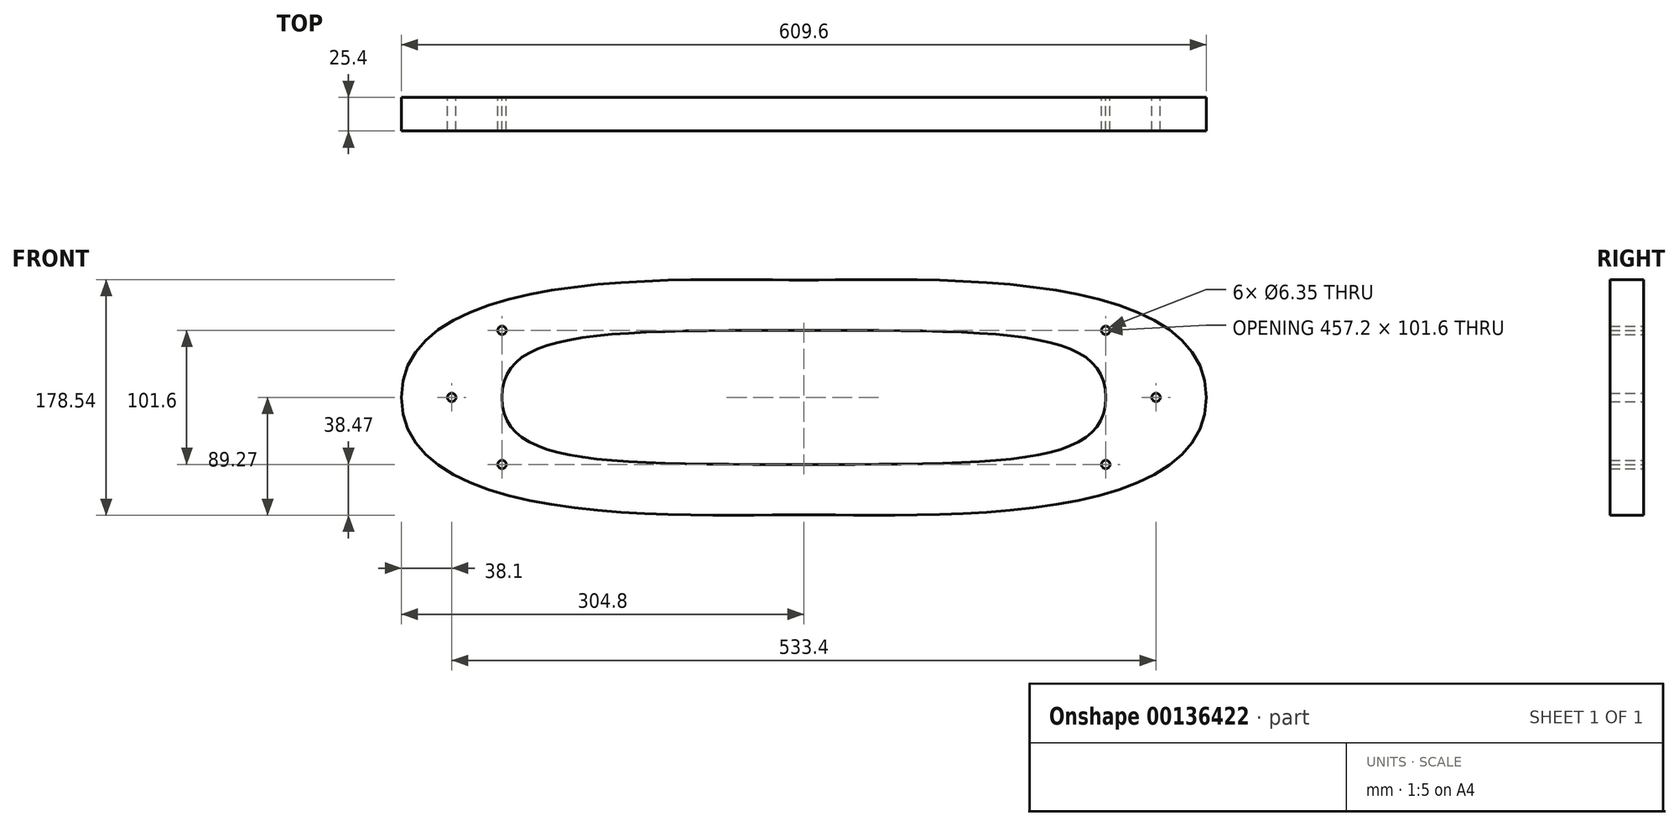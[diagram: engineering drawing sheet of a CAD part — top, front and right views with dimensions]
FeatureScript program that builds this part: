
annotation { "Feature Type Name" : "Feature", "Feature Type Description" : "" }
export const myFeature = defineFeature(function(context is Context, id is Id, definition is map)
    precondition{}
    {
        {
            var Q0;
            Q0=qCreatedBy(makeId("Front.planeOp"),FACE);
            var sketch = newSketch(context, id + "F0", { "sketchPlane" : qUnion([Q0])});
            skLineSegment(sketch, "E0.bottom", {"start": v(228.6, -101.6) * mm, "end": v(-228.6, -101.6) * mm, "construction": true});
            skLineSegment(sketch, "E0.top", {"start": v(228.6, 101.6) * mm, "end": v(-228.6, 101.6) * mm, "construction": true});
            skLineSegment(sketch, "E0.left", {"start": v(228.6, -101.6) * mm, "end": v(228.6, 101.6) * mm, "construction": true});
            skLineSegment(sketch, "E0.right", {"start": v(-228.6, -101.6) * mm, "end": v(-228.6, 101.6) * mm, "construction": true});
            skPoint(sketch, "E0.middle", {"position": v(0, 0) * mm});
            skLineSegment(sketch, "E1", {"start": v(-228.6, 0) * mm, "end": v(228.6, 0) * mm, "construction": true});
            skLineSegment(sketch, "E2", {"start": v(0, 101.6) * mm, "end": v(0, -101.6) * mm, "construction": true});
            skEllipse(sketch, "E3", {"center": v(0, 0) * mm, "majorRadius": 228.6 * mm, "minorRadius": 101.6 * mm, "majorAxis": v(1, 0), "construction": true});
            skLineSegment(sketch, "E4.0", {"start": v(-228.6, 50.8) * mm, "end": v(228.6, 50.8) * mm, "construction": true});
            skFitSpline(sketch, "E5", {"points": [v(-228.6, 0) * mm, v(0, 50.8) * mm], "startDerivative": vector(0, 152.4) * mm, "endDerivative": vector(467.31, 0) * mm});
            skFitSpline(sketch, "E6.MirrorCS", {"points": [v(-228.6, 0) * mm, v(0, -50.8) * mm], "startDerivative": vector(0, -152.4) * mm, "endDerivative": vector(467.31, 0) * mm});
            skFitSpline(sketch, "E7.MirrorCS", {"points": [v(228.6, 0) * mm, v(0, -50.8) * mm], "startDerivative": vector(0, -152.4) * mm, "endDerivative": vector(-467.31, 0) * mm});
            skFitSpline(sketch, "E8.MirrorCS", {"points": [v(228.6, 0) * mm, v(0, 50.8) * mm], "startDerivative": vector(0, 152.4) * mm, "endDerivative": vector(-467.31, 0) * mm});
            skLineSegment(sketch, "E9.0", {"start": v(-304.8, -101.6) * mm, "end": v(-304.8, 101.6) * mm, "construction": true});
            skFitSpline(sketch, "E10", {"points": [v(-304.8, 0) * mm, v(0, 88.9) * mm], "startDerivative": vector(0, 304.8) * mm, "endDerivative": vector(240.47, 1.05) * mm});
            skFitSpline(sketch, "E11.MirrorCS", {"points": [v(-304.8, 0) * mm, v(0, -88.9) * mm], "startDerivative": vector(0, -304.8) * mm, "endDerivative": vector(240.47, -1.05) * mm});
            skFitSpline(sketch, "E12.MirrorCS", {"points": [v(304.8, 0) * mm, v(0, -88.9) * mm], "startDerivative": vector(0, -304.8) * mm, "endDerivative": vector(-240.47, -1.05) * mm});
            skFitSpline(sketch, "E13.MirrorCS", {"points": [v(304.8, 0) * mm, v(0, 88.9) * mm], "startDerivative": vector(0, 304.8) * mm, "endDerivative": vector(-240.47, 1.05) * mm});
            skLineSegment(sketch, "E14.0", {"start": v(-266.7, -101.6) * mm, "end": v(-266.7, 101.6) * mm, "construction": true});
            skLineSegment(sketch, "E15.MirrorCS", {"start": v(-228.6, -50.8) * mm, "end": v(228.6, -50.8) * mm, "construction": true});
            skCircle(sketch, "E16", {"center": v(-228.6, 50.8) * mm, "radius": 3.18 * mm});
            skCircle(sketch, "E17", {"center": v(-266.7, 0) * mm, "radius": 3.18 * mm});
            skCircle(sketch, "E18", {"center": v(-228.6, -50.8) * mm, "radius": 3.18 * mm});
            skCircle(sketch, "E19.MirrorC", {"center": v(228.6, 50.8) * mm, "radius": 3.18 * mm});
            skCircle(sketch, "E20.MirrorC", {"center": v(266.7, 0) * mm, "radius": 3.18 * mm});
            skCircle(sketch, "E21.MirrorC", {"center": v(228.6, -50.8) * mm, "radius": 3.18 * mm});
            skSolve(sketch);
        }
        {
            var Q0;
            Q0 = qSketchRegion(id + "F0", true);
            extrude(context, id + "F1", {"entities" : qUnion([Q0]), "depth" : 25.4 * mm});
        }
    });
